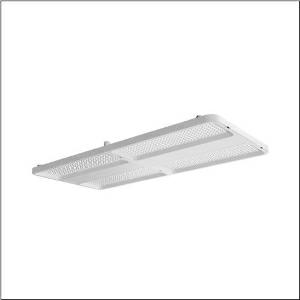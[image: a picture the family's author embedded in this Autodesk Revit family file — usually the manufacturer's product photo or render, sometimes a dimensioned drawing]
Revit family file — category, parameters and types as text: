
# Revit family: highbay_11_maxi_51hn11db4rda
name_source: partatom
category: Lighting Fixtures
units: mm (PartAtom-declared; Revit-internal decimal feet)

## family parameters
Cut with Voids When Loaded = No
Host = Face
Light Source = No
Part Type = Normal
Room Calculation Point = No
Round Connector Dimension = Use Diameter
Shared = No

## types (1)
- --- (1 x LED, 6720 lm, 32.8 W, 4000K)
    Apparent Load = 33 VA
    CIE Flux Codes = 85 97 100 100 100
    Color Rendering = 80
    Color Temperature = 4000K
    Default Elevation = 1800 mm
    Description = high bay luminaire Highbay 11 maxi; direct symmetric narrow distribution, light control with lens of PMMA; UGR ≤ 22 (X = 4H | Y = 8H | S = 0.25H | reflection values 70/50/20); luminous flux: 42.500lm; light colour: 840, colour temperature: 4000K, MacAdam ≤ 2 SDCM (initial), colour rendering: CRI > 80; luminous efficacy: 198,9lm/W; rated service life: 100.000h (L95) at AT= 25°C; control: DALI 2; luminaire connection: terminal, 5-pole, max. 2.5mm² (cable entry for one cable, Ø 8.5..16mm); mains connection: 230..240V, AC/DC 0/50..60Hz; connected load: 213,7W; protection rating (complete): IP66; insulation class (complete): insulation class I (protective earthing); protection symbol: D; impact resistance: IK08; certification: CE, ENEC, VDE, UKCA; luminaire for central battery installations according to EN 60598-2-22, internal wiring halogen-free; luminaire Suitable for use in the food industry according to the specifications of IFS-Food, HACCP and/or BRC; LABS conformity tested according to VDMA 24364:2018-05; housing frame of high-performance plastic PA6, matt traffic white (RAL 9016); cover of PMMA; dimension (LxWxH): 946 x 442 x 72mm; permissible operating ambient temperature: -40..+50°C (reducing of maximum allowable ambient temperature of 5°C with ceiling mounting); packaging unit: 1 piece; (delivery without accessories; please order mounting accessories separately)
    Height = 72 mm  [stored 0.23622 ft]
    Lamp = 1 x LED
    Lamp Light Flux = 6720 lm
    Lamp Power = 32.8 W
    Lamp count = 1
    Length = 946 mm
    Luminous efficacy = 205 lm/W
    Manufacturer = Siteco
    ModVariant = No
    Model = 51HN11DB4RDA
    Mounting Place = Ceiling
    Mounting Type = Pendant
    Number of Poles = 1
    OnlyDefault = Yes
    Power Factor = 1
    Product Name = Highbay 11 maxi
    Product group = high bay luminaire
    ProductGroupID = 902
    Protection Class = Protection class I
    Protection Degree = IP 66
    RLX_Detail_Level = 1
    RLX_Emergency_Light_Flux = 0 lm
    RLX_Emergency_Type = 0
    RLX_Emergency_Type_DB = No
    RlxData = <blob elided: 127189 chars, md5=d19120ba>
    Socket = socket
    Standby Power = 0 W
    System Light Flux = 6720 lm
    System Power = 33 W
    Type Comments = : DC mode (central or group accumulator) initial emergency light level
    Type Image = l_1363244.jpg
    URL = http://relux.com
    VarID = @adj_022133
    Voltage = 0 V
    Weight = 0.00 kg
    Width = 442 mm

note: [stored X ft] marks values corroborated as IEEE doubles in the binary element streams (Revit-internal decimal feet)

## geometry (parser evidence)
native form markers: Blend x4, Sweep x11
no freeform markers — native parametric forms only
